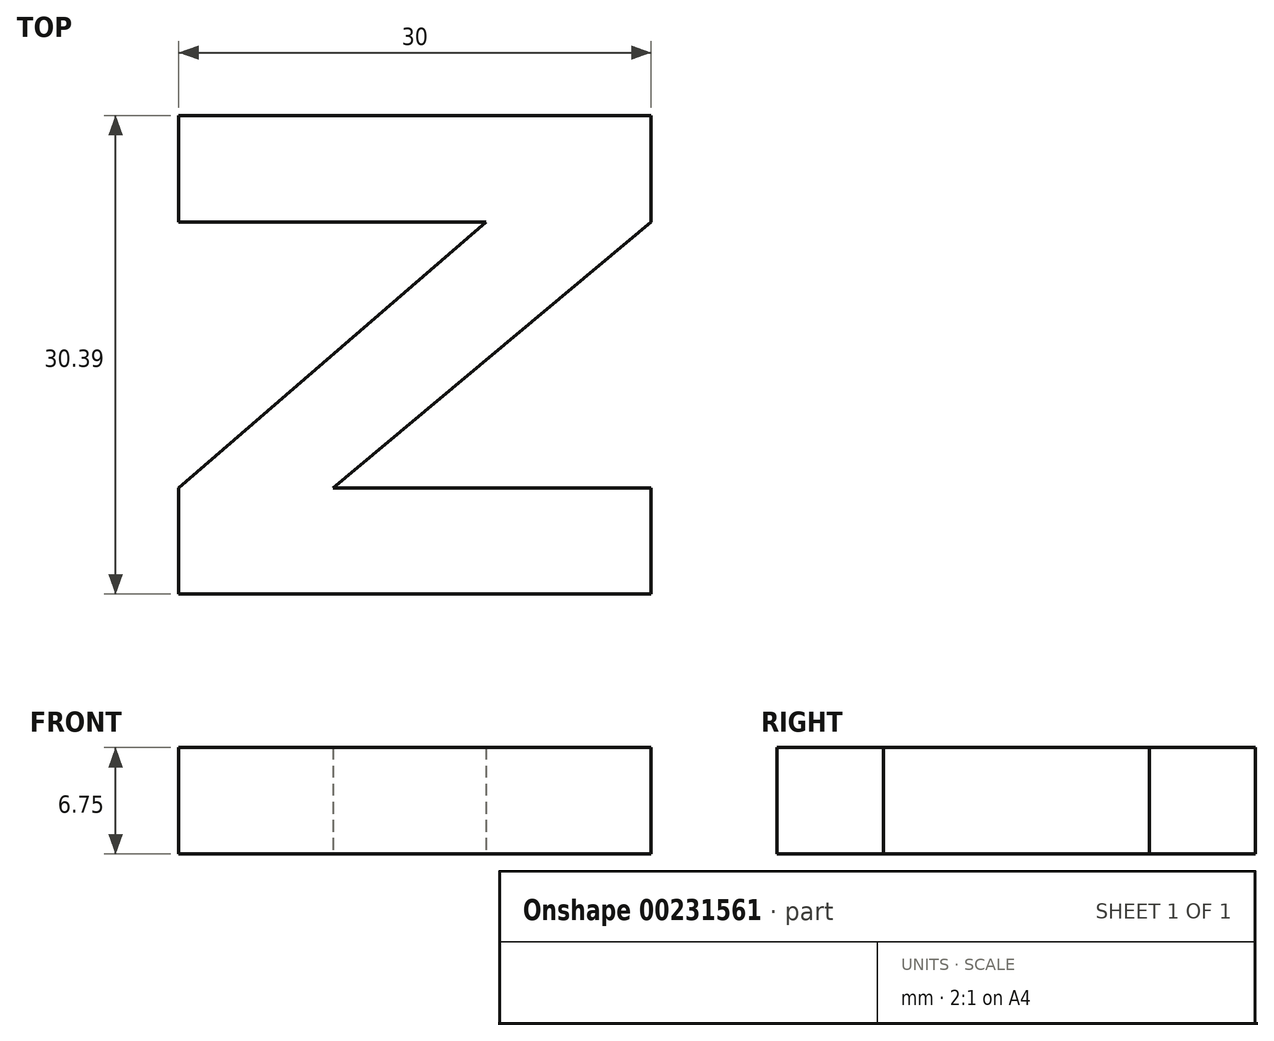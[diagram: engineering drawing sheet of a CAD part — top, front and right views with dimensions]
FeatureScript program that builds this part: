
annotation { "Feature Type Name" : "Feature", "Feature Type Description" : "" }
export const myFeature = defineFeature(function(context is Context, id is Id, definition is map)
    precondition{}
    {
        {
            var Q0;
            Q0=qCreatedBy(makeId("Top.planeOp"),FACE);
            var sketch = newSketch(context, id + "F0", { "sketchPlane" : qUnion([Q0])});
            skLineSegment(sketch, "E0", {"start": v(-53.37, 6.75) * mm, "end": v(-23.37, 6.75) * mm});
            skLineSegment(sketch, "E1", {"start": v(-23.37, 37.14) * mm, "end": v(-53.37, 37.14) * mm});
            skLineSegment(sketch, "E2", {"start": v(-53.37, 37.14) * mm, "end": v(-53.37, 30.39) * mm});
            skLineSegment(sketch, "E3", {"start": v(-53.37, 30.39) * mm, "end": v(-33.86, 30.39) * mm});
            skLineSegment(sketch, "E4", {"start": v(-23.37, 30.39) * mm, "end": v(-23.37, 37.14) * mm});
            skLineSegment(sketch, "E5", {"start": v(-53.37, 6.75) * mm, "end": v(-53.37, 13.5) * mm});
            skLineSegment(sketch, "E6", {"start": v(-23.37, 13.5) * mm, "end": v(-23.37, 6.75) * mm});
            skLineSegment(sketch, "E7.trimOffspring", {"start": v(-43.57, 13.5) * mm, "end": v(-23.37, 13.5) * mm});
            skLineSegment(sketch, "E8", {"start": v(-43.57, 13.5) * mm, "end": v(-23.37, 30.39) * mm});
            skLineSegment(sketch, "E9", {"start": v(-53.37, 13.5) * mm, "end": v(-33.86, 30.39) * mm});
            skSolve(sketch);
        }
        {
            var Q0;
            Q0=makeQuery(id+"F0.imprint","IMPRINT",FACE,{"disambiguationData":[TD([[makeQuery(id+"F0.imprint","IMPRINT",EDGE,{"derivedFrom":sQuery(id+"F0.wireOp",EDGE,"E0")}),1.0]])]});
            extrude(context, id + "F1", {"entities" : qUnion([Q0]), "depth" : 6.75 * mm});
        }
    });
